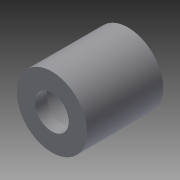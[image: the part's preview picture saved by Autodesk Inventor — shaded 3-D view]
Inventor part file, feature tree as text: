
AUTODESK INVENTOR PART (.ipt)
format: ipt  version: 2014 (Build 180170000, 170)  size: 106,496 bytes
history: native  units: in
note: dims shown in document units (in); Inventor stores cm internally (conversion verified against a paired STEP export)
features: extrude x4, sketch x4
ambient origin geometry x8: Origin, YZ Plane, XZ Plane, XY Plane, X Axis, Y Axis, Z Axis, Center Point
bodies: Solid1 (feature_tree)
feature tree (8):
  extrude  "Extrusion1"  Depth=0.25in TaperAngle=0.0deg
  extrude  "Extrusion2"  Depth=0.247in TaperAngle=0.0deg
  extrude  "Extrusion4"  Depth=0.27in TaperAngle=0.0deg
  extrude  "Extrusion5"  Depth=0.1385in TaperAngle=0.0deg
  sketch  "Sketch1"  dims[d0=0.6325in d1=0.25in d2=0.0in]
  sketch  "Sketch3"  dims[d3=0.1in d5=0.247in d6=0.0in]
  sketch  "Sketch7"  dims[d12=0.5975in d13=0.27in d14=0.0in]
  sketch  "Sketch8"  dims[d15=0.4005in d16=0.1385in d17=0.0in]
